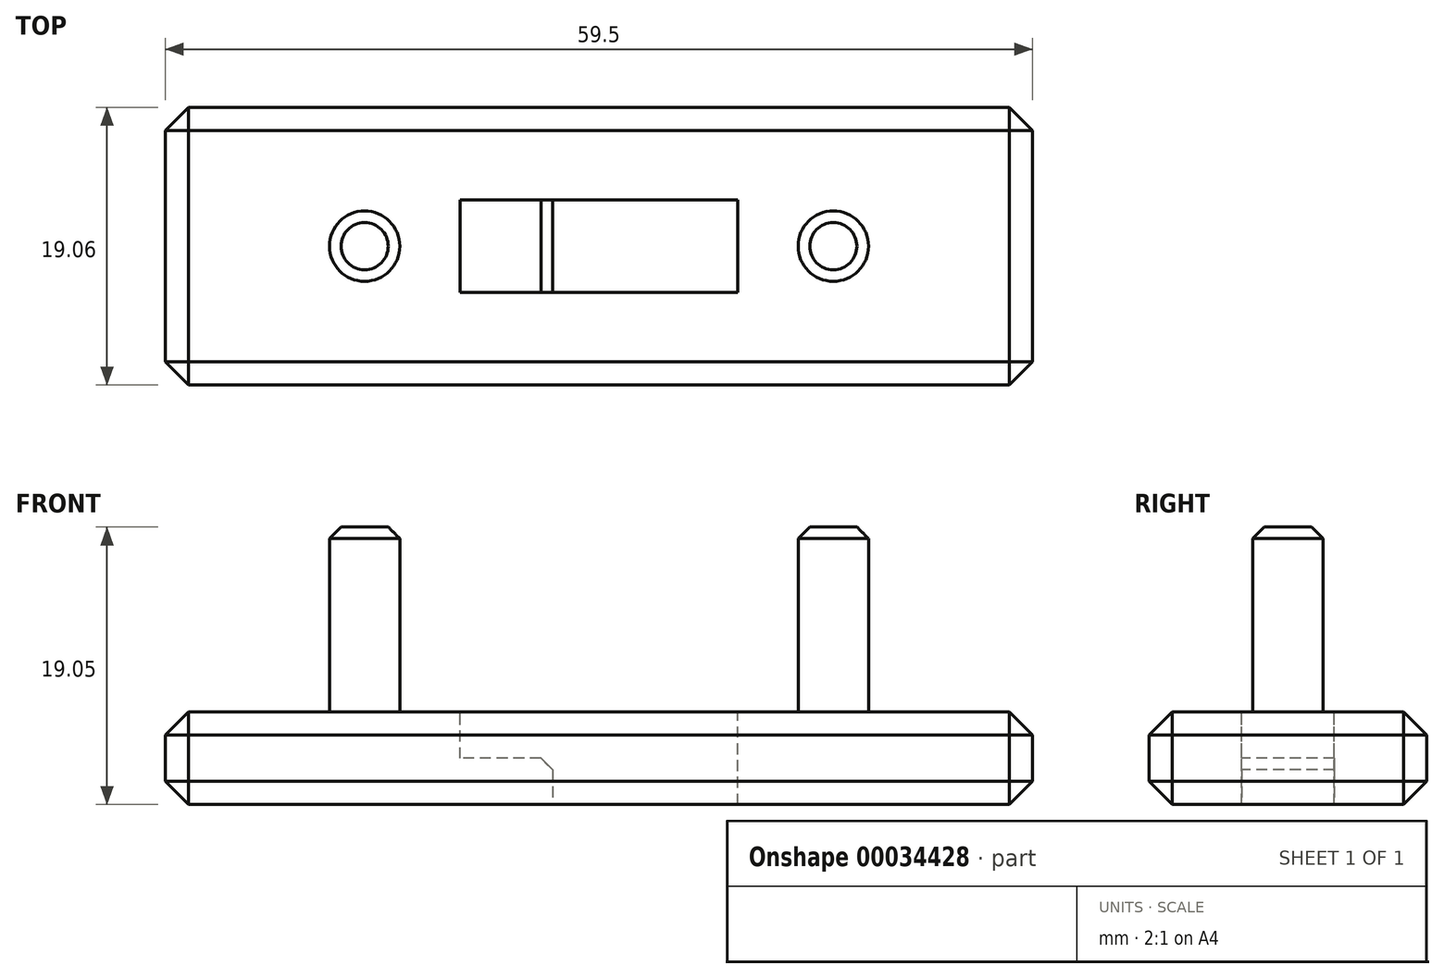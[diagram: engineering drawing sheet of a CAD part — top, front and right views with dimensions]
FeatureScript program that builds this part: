
annotation { "Feature Type Name" : "Feature", "Feature Type Description" : "" }
export const myFeature = defineFeature(function(context is Context, id is Id, definition is map)
    precondition{}
    {
        {
            var Q0;
            Q0=qCreatedBy(makeId("Top.planeOp"),FACE);
            var sketch = newSketch(context, id + "F0", { "sketchPlane" : qUnion([Q0])});
            skLineSegment(sketch, "E0.rect.bottom", {"start": v(29.75, 9.53) * mm, "end": v(-29.75, 9.53) * mm});
            skLineSegment(sketch, "E0.rect.top", {"start": v(29.75, -9.53) * mm, "end": v(-29.75, -9.53) * mm});
            skLineSegment(sketch, "E0.rect.left", {"start": v(29.75, 9.53) * mm, "end": v(29.75, -9.53) * mm});
            skLineSegment(sketch, "E0.rect.right", {"start": v(-29.75, 9.53) * mm, "end": v(-29.75, -9.53) * mm});
            skPoint(sketch, "E0.rect.middle", {"position": v(0, 0) * mm});
            skSolve(sketch);
        }
        {
            var Q0;
            Q0 = qSketchRegion(id + "F0", true);
            extrude(context, id + "F1", {"entities" : qUnion([Q0]), "depth" : 6.35 * mm});
        }
        {
            var Q0;
            Q0=makeQuery(id+"F1.opExtrude","CAP_FACE",FACE,{"disambiguationData":[OSD([sQuery(id+"F0.wireOp",EDGE,"E0.rect.bottom"),sQuery(id+"F0.wireOp",EDGE,"E0.rect.top"),sQuery(id+"F0.wireOp",EDGE,"E0.rect.left"),sQuery(id+"F0.wireOp",EDGE,"E0.rect.right")])],"isStart":false});
            var sketch = newSketch(context, id + "F2", { "sketchPlane" : qUnion([Q0])});
            skCircle(sketch, "E1", {"center": v(-16.08, 0) * mm, "radius": 2.41 * mm});
            skCircle(sketch, "E2", {"center": v(16.08, 0) * mm, "radius": 2.41 * mm});
            skLineSegment(sketch, "E3", {"start": v(0, 0) * mm, "end": v(0, -15.99) * mm, "construction": true});
            skSolve(sketch);
        }
        {
            var Q0;
            Q0 = qSketchRegion(id + "F2", true);
            extrude(context, id + "F3", {"entities" : qUnion([Q0]), "operationType" : NewBodyOperationType.ADD, "depth" : 12.7 * mm});
        }
        {
            var Q0;
            Q0=makeQuery(id+"F1.opExtrude","CAP_FACE",FACE,{"disambiguationData":[OSD([sQuery(id+"F0.wireOp",EDGE,"E0.rect.bottom"),sQuery(id+"F0.wireOp",EDGE,"E0.rect.top"),sQuery(id+"F0.wireOp",EDGE,"E0.rect.left"),sQuery(id+"F0.wireOp",EDGE,"E0.rect.right")])],"isStart":false});
            var sketch = newSketch(context, id + "F4", { "sketchPlane" : qUnion([Q0])});
            skLineSegment(sketch, "E4.rect.bottom", {"start": v(9.53, 3.18) * mm, "end": v(-9.53, 3.18) * mm});
            skLineSegment(sketch, "E4.rect.top", {"start": v(9.53, -3.18) * mm, "end": v(-9.53, -3.18) * mm});
            skLineSegment(sketch, "E4.rect.left", {"start": v(9.53, 3.18) * mm, "end": v(9.53, -3.18) * mm});
            skLineSegment(sketch, "E4.rect.right", {"start": v(-9.53, 3.18) * mm, "end": v(-9.53, -3.18) * mm});
            skPoint(sketch, "E4.rect.middle", {"position": v(0, 0) * mm});
            skSolve(sketch);
        }
        {
            var Q0;
            Q0 = qSketchRegion(id + "F4", true);
            extrude(context, id + "F5", {"entities" : qUnion([Q0]), "operationType" : NewBodyOperationType.REMOVE, "oppositeDirection" : true, "depth" : 3.17 * mm});
        }
        {
            var Q0;
            Q0=makeQuery(id+"F1.opExtrude","CAP_FACE",FACE,{"disambiguationData":[OSD([sQuery(id+"F0.wireOp",EDGE,"E0.rect.bottom"),sQuery(id+"F0.wireOp",EDGE,"E0.rect.top"),sQuery(id+"F0.wireOp",EDGE,"E0.rect.left"),sQuery(id+"F0.wireOp",EDGE,"E0.rect.right")])],"isStart":true});
            var sketch = newSketch(context, id + "F6", { "sketchPlane" : qUnion([Q0])});
            skLineSegment(sketch, "E5.0", {"start": v(9.53, -3.18) * mm, "end": v(9.53, 3.18) * mm});
            skLineSegment(sketch, "E6", {"start": v(9.53, 3.18) * mm, "end": v(-3.17, 3.18) * mm});
            skLineSegment(sketch, "E7", {"start": v(-3.17, 3.17) * mm, "end": v(-3.17, -3.18) * mm});
            skLineSegment(sketch, "E8", {"start": v(-3.17, -3.18) * mm, "end": v(9.53, -3.18) * mm});
            skSolve(sketch);
        }
        {
            var Q0;
            Q0 = qSketchRegion(id + "F6", true);
            extrude(context, id + "F7", {"entities" : qUnion([Q0]), "operationType" : NewBodyOperationType.REMOVE, "endBound" : BoundingType.THROUGH_ALL, "oppositeDirection" : true, "depth" : 25.4 * mm});
        }
        {
            var Q0;
            Q0=makeQuery(id+"F7.boolean.opBoolean","INTERSECT",EDGE,{"derivedFrom":[makeQuery(id+"F5.boolean.opBoolean","COPY",FACE,{"derivedFrom":makeQuery(id+"F5.opExtrude","CAP_FACE",FACE,{"disambiguationData":[OSD([sQuery(id+"F4.wireOp",EDGE,"E4.rect.bottom"),sQuery(id+"F4.wireOp",EDGE,"E4.rect.top"),sQuery(id+"F4.wireOp",EDGE,"E4.rect.left"),sQuery(id+"F4.wireOp",EDGE,"E4.rect.right")])],"isStart":false})}),makeQuery(id+"F7.opExtrude","SWEPT_FACE",FACE,{"disambiguationData":[OSD([sQuery(id+"F6.wireOp",EDGE,"E7")])]})]});
            var Q1;
            Q1=makeQuery(id+"F7.boolean.opBoolean","COPY",EDGE,{"derivedFrom":makeQuery(id+"F7.opExtrude","CAP_EDGE",EDGE,{"disambiguationData":[OSD([sQuery(id+"F6.wireOp",EDGE,"E7")])],"isStart":true})});
            var Q2;
            Q2=makeQuery(id+"F5.boolean.opBoolean","COPY",EDGE,{"derivedFrom":makeQuery(id+"F5.opExtrude","CAP_EDGE",EDGE,{"disambiguationData":[OSD([sQuery(id+"F4.wireOp",EDGE,"E4.rect.bottom")])],"isStart":true})});
            var Q3;
            Q3=makeQuery(id+"F5.boolean.opBoolean","COPY",EDGE,{"derivedFrom":makeQuery(id+"F5.opExtrude","CAP_EDGE",EDGE,{"disambiguationData":[OSD([sQuery(id+"F4.wireOp",EDGE,"E4.rect.left")])],"isStart":true})});
            var Q4;
            Q4=makeQuery(id+"F5.boolean.opBoolean","COPY",EDGE,{"derivedFrom":makeQuery(id+"F5.opExtrude","CAP_EDGE",EDGE,{"disambiguationData":[OSD([sQuery(id+"F4.wireOp",EDGE,"E4.rect.top")])],"isStart":true})});
            var Q5;
            Q5=makeQuery(id+"F5.boolean.opBoolean","COPY",EDGE,{"derivedFrom":makeQuery(id+"F5.opExtrude","CAP_EDGE",EDGE,{"disambiguationData":[OSD([sQuery(id+"F4.wireOp",EDGE,"E4.rect.right")])],"isStart":true})});
            chamfer(context, id + "F8", {"entities" : qUnion([Q0, Q1, Q2, Q3, Q4, Q5]), "width" : 0.8 * mm, "tangentPropagation" : true});
        }
        {
            var Q0;
            Q0=makeQuery(id+"F1.opExtrude","SWEPT_FACE",FACE,{"disambiguationData":[OSD([sQuery(id+"F0.wireOp",EDGE,"E0.rect.top")])]});
            var Q1;
            Q1=makeQuery(id+"F1.opExtrude","SWEPT_FACE",FACE,{"disambiguationData":[OSD([sQuery(id+"F0.wireOp",EDGE,"E0.rect.left")])]});
            var Q2;
            Q2=makeQuery(id+"F1.opExtrude","SWEPT_FACE",FACE,{"disambiguationData":[OSD([sQuery(id+"F0.wireOp",EDGE,"E0.rect.bottom")])]});
            var Q3;
            Q3=makeQuery(id+"F1.opExtrude","SWEPT_FACE",FACE,{"disambiguationData":[OSD([sQuery(id+"F0.wireOp",EDGE,"E0.rect.right")])]});
            chamfer(context, id + "F9", {"entities" : qUnion([Q0, Q1, Q2, Q3]), "width" : 1.59 * mm, "tangentPropagation" : true});
        }
        {
            var Q0;
            Q0=makeQuery(id+"F3.opExtrude","CAP_EDGE",EDGE,{"disambiguationData":[OSD([sQuery(id+"F2.wireOp",EDGE,"E2")])],"isStart":false});
            var Q1;
            Q1=makeQuery(id+"F3.opExtrude","CAP_EDGE",EDGE,{"disambiguationData":[OSD([sQuery(id+"F2.wireOp",EDGE,"E1")])],"isStart":false});
            chamfer(context, id + "F10", {"entities" : qUnion([Q0, Q1]), "width" : 0.8 * mm, "tangentPropagation" : true});
        }
    });
